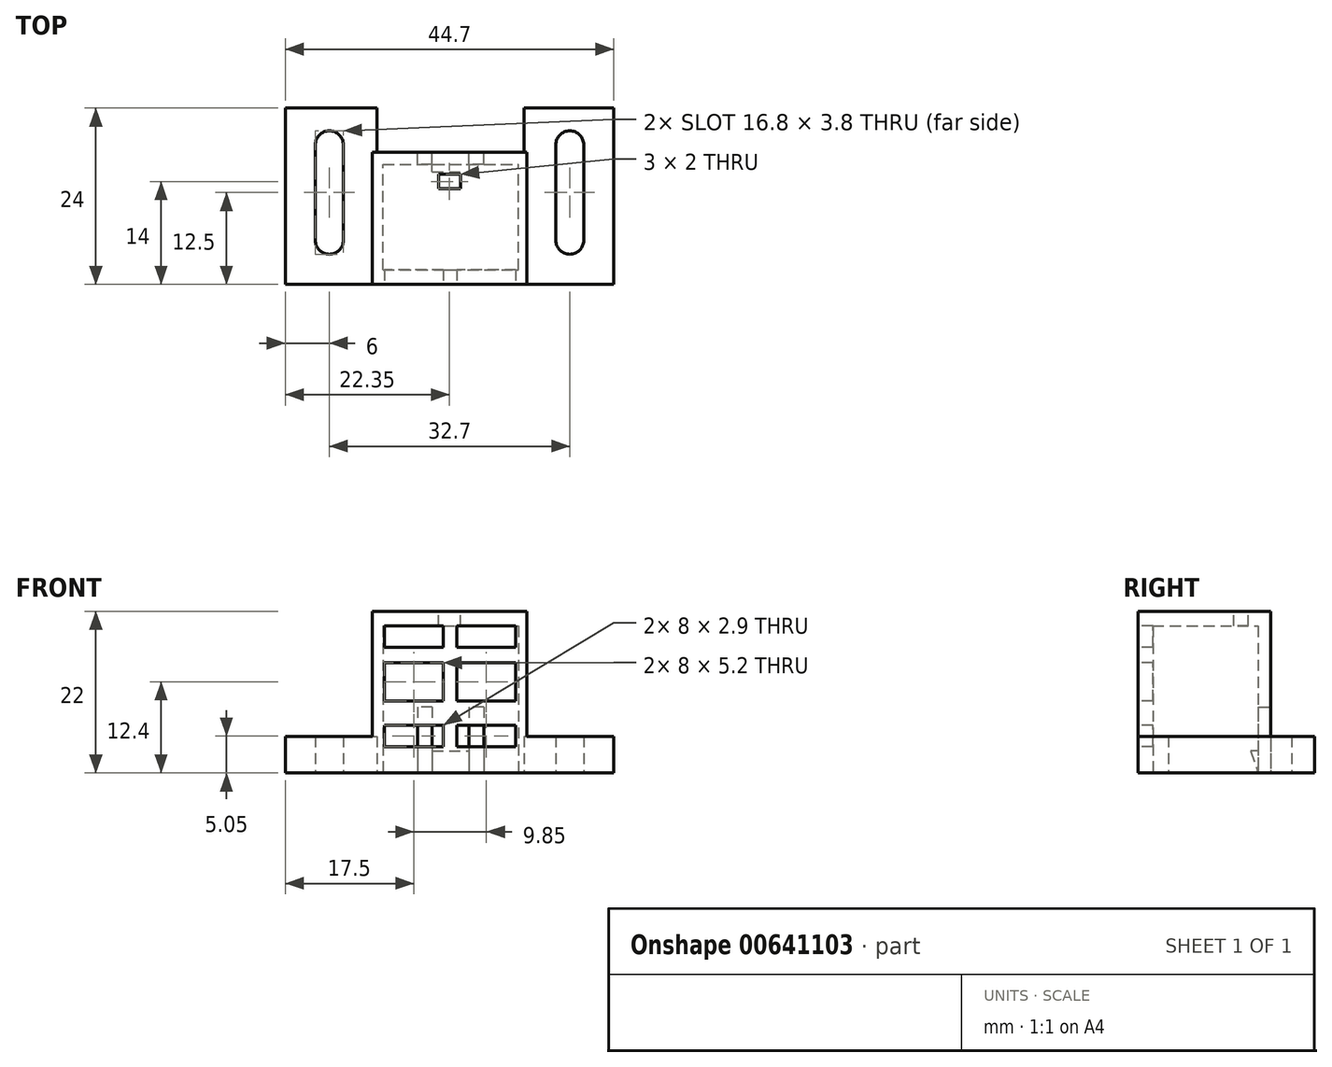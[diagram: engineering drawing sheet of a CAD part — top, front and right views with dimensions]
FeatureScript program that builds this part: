
annotation { "Feature Type Name" : "Feature", "Feature Type Description" : "" }
export const myFeature = defineFeature(function(context is Context, id is Id, definition is map)
    precondition{}
    {
        {
            var Q0;
            Q0=qCreatedBy(makeId("Top.planeOp"),FACE);
            var sketch = newSketch(context, id + "F0", { "sketchPlane" : qUnion([Q0])});
            skLineSegment(sketch, "E0.bottom", {"start": v(-22.5, 24) * mm, "end": v(-10, 24) * mm});
            skLineSegment(sketch, "E0.top", {"start": v(-22.5, 0) * mm, "end": v(22.2, 0) * mm});
            skLineSegment(sketch, "E0.left", {"start": v(-22.5, 24) * mm, "end": v(-22.5, 0) * mm});
            skLineSegment(sketch, "E0.right", {"start": v(22.2, 24) * mm, "end": v(22.2, 0) * mm});
            skLineSegment(sketch, "E1", {"start": v(-16.5, -5.37) * mm, "end": v(-16.5, 26.83) * mm, "construction": true});
            skLineSegment(sketch, "E2", {"start": v(16.2, -5.76) * mm, "end": v(16.2, 27.78) * mm, "construction": true});
            skLineSegment(sketch, "E3.bottom", {"start": v(-18.4, 19) * mm, "end": v(-14.6, 19) * mm});
            skLineSegment(sketch, "E3.top", {"start": v(-18.4, 6) * mm, "end": v(-14.6, 6) * mm});
            skLineSegment(sketch, "E3.left", {"start": v(-18.4, 19) * mm, "end": v(-18.4, 6) * mm});
            skLineSegment(sketch, "E3.right", {"start": v(-14.6, 19) * mm, "end": v(-14.6, 6) * mm});
            skLineSegment(sketch, "E4.bottom", {"start": v(14.3, 19) * mm, "end": v(18.1, 19) * mm});
            skLineSegment(sketch, "E4.top", {"start": v(14.3, 6) * mm, "end": v(18.1, 6) * mm});
            skLineSegment(sketch, "E4.left", {"start": v(14.3, 19) * mm, "end": v(14.3, 6) * mm});
            skLineSegment(sketch, "E4.right", {"start": v(18.1, 19) * mm, "end": v(18.1, 6) * mm});
            skLineSegment(sketch, "E5.bottom", {"start": v(-9.2, 2) * mm, "end": v(9.2, 2) * mm});
            skLineSegment(sketch, "E5.top", {"start": v(-9.2, 16.3) * mm, "end": v(9.2, 16.3) * mm});
            skLineSegment(sketch, "E5.left", {"start": v(-9.2, 2) * mm, "end": v(-9.2, 16.3) * mm});
            skLineSegment(sketch, "E5.right", {"start": v(9.2, 2) * mm, "end": v(9.2, 16.3) * mm});
            skLineSegment(sketch, "E6", {"start": v(-10, 24) * mm, "end": v(-10, 18) * mm});
            skLineSegment(sketch, "E7", {"start": v(-10, 18) * mm, "end": v(10, 18) * mm});
            skLineSegment(sketch, "E8", {"start": v(10, 18) * mm, "end": v(10, 24) * mm});
            skArc(sketch, "E9", {"start": v(-18.4, 19) * mm, "mid": v(-16.5, 20.9) * mm, "end": v(-14.6, 19) * mm});
            skArc(sketch, "E10", {"start": v(-18.4, 6) * mm, "mid": v(-16.5, 4.1) * mm, "end": v(-14.6, 6) * mm});
            skArc(sketch, "E11", {"start": v(14.3, 6) * mm, "mid": v(16.2, 4.1) * mm, "end": v(18.1, 6) * mm});
            skArc(sketch, "E12", {"start": v(14.3, 19) * mm, "mid": v(16.2, 20.9) * mm, "end": v(18.1, 19) * mm});
            skLineSegment(sketch, "E13", {"start": v(10, 24) * mm, "end": v(22.2, 24) * mm});
            skSolve(sketch);
        }
        {
            var Q0;
            Q0=makeQuery(id+"F0.imprint","IMPRINT",FACE,{"disambiguationData":[TD([[makeQuery(id+"F0.imprint","IMPRINT",EDGE,{"derivedFrom":sQuery(id+"F0.wireOp",EDGE,"E0.bottom")}),-1.0]])]});
            extrude(context, id + "F1", {"entities" : qUnion([Q0]), "depth" : 5 * mm, "offsetDistance" : 25 * mm});
        }
        {
            var Q0;
            Q0=makeQuery(id+"F1.opExtrude","CAP_FACE",FACE,{"disambiguationData":[OSD([sQuery(id+"F0.wireOp",EDGE,"E0.bottom"),sQuery(id+"F0.wireOp",EDGE,"E0.top"),sQuery(id+"F0.wireOp",EDGE,"E0.left"),sQuery(id+"F0.wireOp",EDGE,"E0.right"),sQuery(id+"F0.wireOp",EDGE,"E3.left"),sQuery(id+"F0.wireOp",EDGE,"E3.right"),sQuery(id+"F0.wireOp",EDGE,"E4.left"),sQuery(id+"F0.wireOp",EDGE,"E4.right"),sQuery(id+"F0.wireOp",EDGE,"E5.bottom"),sQuery(id+"F0.wireOp",EDGE,"E5.top"),sQuery(id+"F0.wireOp",EDGE,"E5.left"),sQuery(id+"F0.wireOp",EDGE,"E5.right"),sQuery(id+"F0.wireOp",EDGE,"E6"),sQuery(id+"F0.wireOp",EDGE,"E7"),sQuery(id+"F0.wireOp",EDGE,"E8"),sQuery(id+"F0.wireOp",EDGE,"E9"),sQuery(id+"F0.wireOp",EDGE,"E10"),sQuery(id+"F0.wireOp",EDGE,"E11"),sQuery(id+"F0.wireOp",EDGE,"E12"),sQuery(id+"F0.wireOp",EDGE,"E13")])],"isStart":false});
            var sketch = newSketch(context, id + "F2", { "sketchPlane" : qUnion([Q0])});
            skLineSegment(sketch, "E14", {"start": v(-10.65, 0) * mm, "end": v(-10.65, 18) * mm});
            skLineSegment(sketch, "E15", {"start": v(10.35, 0) * mm, "end": v(10.35, 18) * mm});
            skLineSegment(sketch, "E16", {"start": v(10, 18) * mm, "end": v(10.35, 18) * mm});
            skLineSegment(sketch, "E17", {"start": v(-10, 18) * mm, "end": v(-10.65, 18) * mm});
            skSolve(sketch);
        }
        {
            var Q0;
            {var subQ0=sQuery(id+"F2.wireOp",EDGE,"E14");Q0=makeQuery(id+"F2.imprint","IMPRINT",FACE,{"disambiguationData":[TD([[makeQuery(id+"F2.imprint","IMPRINT",EDGE,{"derivedFrom":subQ0}),-1.0]])]});}
            extrude(context, id + "F3", {"entities" : qUnion([Q0]), "operationType" : NewBodyOperationType.ADD, "depth" : 15 * mm, "offsetDistance" : 25 * mm});
        }
        {
            var Q0;
            Q0=makeQuery(id+"F3.opExtrude","CAP_FACE",FACE,{"disambiguationData":[OSD([sQuery(id+"F0.wireOp",EDGE,"E0.top"),sQuery(id+"F0.wireOp",EDGE,"E5.bottom"),sQuery(id+"F0.wireOp",EDGE,"E5.top"),sQuery(id+"F0.wireOp",EDGE,"E5.left"),sQuery(id+"F0.wireOp",EDGE,"E5.right"),sQuery(id+"F0.wireOp",EDGE,"E7"),sQuery(id+"F2.wireOp",EDGE,"E14"),sQuery(id+"F2.wireOp",EDGE,"E15"),sQuery(id+"F2.wireOp",EDGE,"E16"),sQuery(id+"F2.wireOp",EDGE,"E17")])],"isStart":false});
            var sketch = newSketch(context, id + "F4", { "sketchPlane" : qUnion([Q0])});
            skLineSegment(sketch, "E18.bottom", {"start": v(-10.65, 18) * mm, "end": v(10.35, 18) * mm});
            skLineSegment(sketch, "E18.top", {"start": v(-10.65, 0) * mm, "end": v(10.35, 0) * mm});
            skLineSegment(sketch, "E18.left", {"start": v(-10.65, 18) * mm, "end": v(-10.65, 0) * mm});
            skLineSegment(sketch, "E18.right", {"start": v(10.35, 18) * mm, "end": v(10.35, 0) * mm});
            skSolve(sketch);
        }
        {
            var Q0;
            Q0 = qSketchRegion(id + "F4", true);
            extrude(context, id + "F5", {"entities" : qUnion([Q0]), "operationType" : NewBodyOperationType.ADD, "depth" : 2 * mm, "offsetDistance" : 25 * mm});
        }
        {
            var Q0;
            {var subQ0=sQuery(id+"F0.wireOp",EDGE,"E0.top");Q0=makeQuery(id+"F5.boolean.opBoolean","MERGE",FACE,{"derivedFrom":[makeQuery(id+"F3.boolean.opBoolean","MERGE",FACE,{"derivedFrom":[makeQuery(id+"F1.opExtrude","SWEPT_FACE",FACE,{"disambiguationData":[OSD([subQ0])]}),makeQuery(id+"F3.opExtrude","SWEPT_FACE",FACE,{"disambiguationData":[OSD([subQ0])]})]}),makeQuery(id+"F5.opExtrude","SWEPT_FACE",FACE,{"disambiguationData":[OSD([sQuery(id+"F4.wireOp",EDGE,"E18.top")])]})]});}
            var sketch = newSketch(context, id + "F6", { "sketchPlane" : qUnion([Q0])});
            skLineSegment(sketch, "E19.bottom", {"start": v(-9, 20) * mm, "end": v(-1, 20) * mm});
            skLineSegment(sketch, "E19.top", {"start": v(-9, 17.1) * mm, "end": v(-1, 17.1) * mm});
            skLineSegment(sketch, "E19.left", {"start": v(-9, 20) * mm, "end": v(-9, 17.1) * mm});
            skLineSegment(sketch, "E19.right", {"start": v(-1, 20) * mm, "end": v(-1, 17.1) * mm});
            skLineSegment(sketch, "E20.bottom", {"start": v(0.85, 20) * mm, "end": v(8.85, 20) * mm});
            skLineSegment(sketch, "E20.top", {"start": v(0.85, 17.1) * mm, "end": v(8.85, 17.1) * mm});
            skLineSegment(sketch, "E20.left", {"start": v(0.85, 20) * mm, "end": v(0.85, 17.1) * mm});
            skLineSegment(sketch, "E20.right", {"start": v(8.85, 20) * mm, "end": v(8.85, 17.1) * mm});
            skLineSegment(sketch, "E21.bottom", {"start": v(-9, 15) * mm, "end": v(-1, 15) * mm});
            skLineSegment(sketch, "E21.top", {"start": v(-9, 9.8) * mm, "end": v(-1, 9.8) * mm});
            skLineSegment(sketch, "E21.left", {"start": v(-9, 15) * mm, "end": v(-9, 9.8) * mm});
            skLineSegment(sketch, "E21.right", {"start": v(-1, 15) * mm, "end": v(-1, 9.8) * mm});
            skLineSegment(sketch, "E22.bottom", {"start": v(0.85, 15) * mm, "end": v(8.85, 15) * mm});
            skLineSegment(sketch, "E22.top", {"start": v(0.85, 9.8) * mm, "end": v(8.85, 9.8) * mm});
            skLineSegment(sketch, "E22.left", {"start": v(0.85, 15) * mm, "end": v(0.85, 9.8) * mm});
            skLineSegment(sketch, "E22.right", {"start": v(8.85, 15) * mm, "end": v(8.85, 9.8) * mm});
            skLineSegment(sketch, "E23.bottom", {"start": v(-9, 6.5) * mm, "end": v(-1, 6.5) * mm});
            skLineSegment(sketch, "E23.top", {"start": v(-9, 3.6) * mm, "end": v(-1, 3.6) * mm});
            skLineSegment(sketch, "E23.left", {"start": v(-9, 6.5) * mm, "end": v(-9, 3.6) * mm});
            skLineSegment(sketch, "E23.right", {"start": v(-1, 6.5) * mm, "end": v(-1, 3.6) * mm});
            skLineSegment(sketch, "E24.bottom", {"start": v(0.85, 6.5) * mm, "end": v(8.85, 6.5) * mm});
            skLineSegment(sketch, "E24.top", {"start": v(0.85, 3.6) * mm, "end": v(8.85, 3.6) * mm});
            skLineSegment(sketch, "E24.left", {"start": v(0.85, 6.5) * mm, "end": v(0.85, 3.6) * mm});
            skLineSegment(sketch, "E24.right", {"start": v(8.85, 6.5) * mm, "end": v(8.85, 3.6) * mm});
            skSolve(sketch);
        }
        {
            var Q0;
            Q0 = qSketchRegion(id + "F6", true);
            extrude(context, id + "F7", {"entities" : qUnion([Q0]), "operationType" : NewBodyOperationType.REMOVE, "oppositeDirection" : true, "depth" : 3 * mm, "offsetDistance" : 25 * mm});
        }
        {
            var Q0;
            {var subQ0=sQuery(id+"F0.wireOp",EDGE,"E7");Q0=makeQuery(id+"F5.boolean.opBoolean","MERGE",FACE,{"derivedFrom":[makeQuery(id+"F3.boolean.opBoolean","MERGE",FACE,{"derivedFrom":[makeQuery(id+"F1.opExtrude","SWEPT_FACE",FACE,{"disambiguationData":[OSD([subQ0])]}),makeQuery(id+"F3.opExtrude","SWEPT_FACE",FACE,{"disambiguationData":[OSD([subQ0,sQuery(id+"F2.wireOp",EDGE,"E16"),sQuery(id+"F2.wireOp",EDGE,"E17")])]})]}),makeQuery(id+"F5.opExtrude","SWEPT_FACE",FACE,{"disambiguationData":[OSD([sQuery(id+"F4.wireOp",EDGE,"E18.bottom")])]})]});}
            var sketch = newSketch(context, id + "F8", { "sketchPlane" : qUnion([Q0])});
            skLineSegment(sketch, "E25.bottom", {"start": v(-4.5, 9) * mm, "end": v(-2.5, 9) * mm});
            skLineSegment(sketch, "E25.top", {"start": v(-4.5, -2.25) * mm, "end": v(-2.5, -2.25) * mm});
            skLineSegment(sketch, "E25.left", {"start": v(-4.5, 9) * mm, "end": v(-4.5, -2.25) * mm});
            skLineSegment(sketch, "E25.right", {"start": v(-2.5, 9) * mm, "end": v(-2.5, -2.25) * mm});
            skLineSegment(sketch, "E26.bottom", {"start": v(2.5, 9) * mm, "end": v(4.5, 9) * mm});
            skLineSegment(sketch, "E26.top", {"start": v(2.5, -2.25) * mm, "end": v(4.5, -2.25) * mm});
            skLineSegment(sketch, "E26.left", {"start": v(2.5, 9) * mm, "end": v(2.5, -2.25) * mm});
            skLineSegment(sketch, "E26.right", {"start": v(4.5, 9) * mm, "end": v(4.5, -2.25) * mm});
            skSolve(sketch);
        }
        {
            var Q0;
            Q0 = qSketchRegion(id + "F8", true);
            extrude(context, id + "F9", {"entities" : qUnion([Q0]), "operationType" : NewBodyOperationType.REMOVE, "oppositeDirection" : true, "depth" : 3 * mm, "offsetDistance" : 25 * mm});
        }
        {
            var Q0;
            Q0=makeQuery(id+"F9.boolean.opBoolean","COPY",FACE,{"derivedFrom":makeQuery(id+"F9.opExtrude","SWEPT_FACE",FACE,{"disambiguationData":[OSD([sQuery(id+"F8.wireOp",EDGE,"E25.right")])]})});
            var sketch = newSketch(context, id + "F10", { "sketchPlane" : qUnion([Q0])});
            skLineSegment(sketch, "E27", {"start": v(16.3, 3) * mm, "end": v(15.3, 3) * mm});
            skLineSegment(sketch, "E28", {"start": v(15.3, 3) * mm, "end": v(16.3, 0) * mm});
            skLineSegment(sketch, "E29", {"start": v(16.3, 0) * mm, "end": v(16.3, 3) * mm});
            skSolve(sketch);
        }
        {
            var Q0;
            Q0=makeQuery(id+"F10.imprint","IMPRINT",FACE,{"disambiguationData":[TD([[makeQuery(id+"F10.imprint","IMPRINT",EDGE,{"derivedFrom":sQuery(id+"F10.wireOp",EDGE,"E27")}),1.0]])]});
            extrude(context, id + "F11", {"entities" : qUnion([Q0]), "operationType" : NewBodyOperationType.ADD, "oppositeDirection" : true, "depth" : 5 * mm, "offsetDistance" : 25 * mm});
        }
        {
            var Q0;
            Q0=makeQuery(id+"F5.opExtrude","CAP_FACE",FACE,{"disambiguationData":[OSD([sQuery(id+"F4.wireOp",EDGE,"E18.bottom"),sQuery(id+"F4.wireOp",EDGE,"E18.top"),sQuery(id+"F4.wireOp",EDGE,"E18.left"),sQuery(id+"F4.wireOp",EDGE,"E18.right")])],"isStart":false});
            var sketch = newSketch(context, id + "F12", { "sketchPlane" : qUnion([Q0])});
            skLineSegment(sketch, "E30.bottom", {"start": v(-1.65, 15) * mm, "end": v(1.35, 15) * mm});
            skLineSegment(sketch, "E30.top", {"start": v(-1.65, 13) * mm, "end": v(1.35, 13) * mm});
            skLineSegment(sketch, "E30.left", {"start": v(-1.65, 15) * mm, "end": v(-1.65, 13) * mm});
            skLineSegment(sketch, "E30.right", {"start": v(1.35, 15) * mm, "end": v(1.35, 13) * mm});
            skSolve(sketch);
        }
        {
            var Q0;
            Q0=makeQuery(id+"F12.imprint","IMPRINT",FACE,{"disambiguationData":[TD([[makeQuery(id+"F12.imprint","IMPRINT",EDGE,{"derivedFrom":sQuery(id+"F12.wireOp",EDGE,"E30.bottom")}),-1.0]])]});
            extrude(context, id + "F13", {"entities" : qUnion([Q0]), "operationType" : NewBodyOperationType.REMOVE, "oppositeDirection" : true, "depth" : 5 * mm, "offsetDistance" : 25 * mm});
        }
    });
